# Revit family: TSL_US - TSL46 - Double Toilet Roll Holder
name_source: partatom
category: Specialty Equipment
units: mm (PartAtom-declared; Revit-internal decimal feet)

## family parameters
Always vertical = Yes
Cut with Voids When Loaded = No
Part Type = Normal
Room Calculation Point = No
Round Connector Dimension = Use Diameter
Shared = No
Work Plane-Based = No

## types (5) — shared parameters
Assembly Code = C1030200
Default Elevation = 0' - 0"
Description = The TSL.46 is a double toilet roll holder with a concealed fixing, constructed from stainless steel.
Keynote = 10 28 00.A2
Manufacturer = The Splash Lab
Type Comments = DOUBLE TOILET ROLL HOLDER
Type Image = <None>
URL = https://thesplashlab.com

## per-type parameters (varying)
| type | Model | TSL Material 01 |
| TSL.46.CS - Satin | TSL.46.CS | TSL - Material - Satin |
| TSL.46.CP - Copper | TSL.46.CP | TSL - Material - Copper |
| TSL.46.BR - Brass | TSL.46.BR | TSL - Material - Brass |
| TSL.46.BK - Black | TSL.46.BK | TSL - Material - Black |
| TSL.46.BZ - Bronze | TSL.46.BZ | TSL - Material - Bronze |

## geometry (parser evidence)
native form markers: Sweep x2
no freeform markers — native parametric forms only
